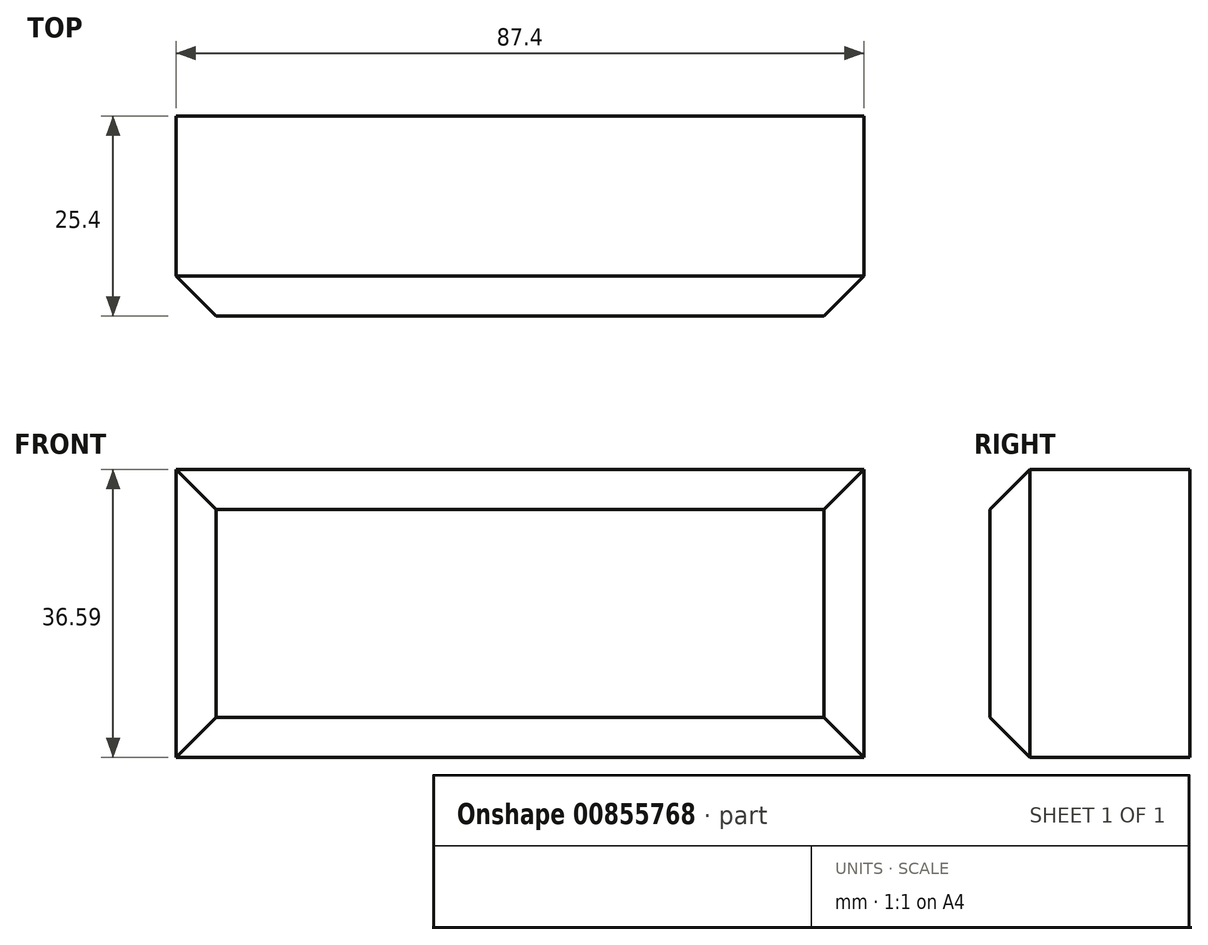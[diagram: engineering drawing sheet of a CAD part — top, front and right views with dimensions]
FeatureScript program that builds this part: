
annotation { "Feature Type Name" : "Feature", "Feature Type Description" : "" }
export const myFeature = defineFeature(function(context is Context, id is Id, definition is map)
    precondition{}
    {
        {
            var Q0;
            Q0=qCreatedBy(makeId("Front.planeOp"),FACE);
            var sketch = newSketch(context, id + "F0", { "sketchPlane" : qUnion([Q0])});
            skLineSegment(sketch, "E0.bottom", {"start": v(-30.78, 17.9) * mm, "end": v(56.62, 17.9) * mm});
            skLineSegment(sketch, "E0.top", {"start": v(-30.78, -18.7) * mm, "end": v(56.62, -18.7) * mm});
            skLineSegment(sketch, "E0.left", {"start": v(-30.78, 17.9) * mm, "end": v(-30.78, -18.7) * mm});
            skLineSegment(sketch, "E0.right", {"start": v(56.62, 17.9) * mm, "end": v(56.62, -18.7) * mm});
            skSolve(sketch);
        }
        {
            var Q0;
            Q0 = qSketchRegion(id + "F0", true);
            extrude(context, id + "F1", {"entities" : qUnion([Q0]), "depth" : 25.4 * mm, "offsetDistance" : 25.4 * mm});
        }
        {
            var Q0;
            Q0=makeQuery(id+"F1.opExtrude","CAP_EDGE",EDGE,{"disambiguationData":[OSD([sQuery(id+"F0.wireOp",EDGE,"E0.bottom")])],"isStart":false});
            var Q1;
            Q1=makeQuery(id+"F1.opExtrude","CAP_EDGE",EDGE,{"disambiguationData":[OSD([sQuery(id+"F0.wireOp",EDGE,"E0.left")])],"isStart":false});
            var Q2;
            Q2=makeQuery(id+"F1.opExtrude","CAP_EDGE",EDGE,{"disambiguationData":[OSD([sQuery(id+"F0.wireOp",EDGE,"E0.right")])],"isStart":false});
            var Q3;
            Q3=makeQuery(id+"F1.opExtrude","CAP_EDGE",EDGE,{"disambiguationData":[OSD([sQuery(id+"F0.wireOp",EDGE,"E0.top")])],"isStart":false});
            chamfer(context, id + "F2", {"entities" : qUnion([Q0, Q1, Q2, Q3]), "width" : 5.08 * mm, "tangentPropagation" : true});
        }
    });
